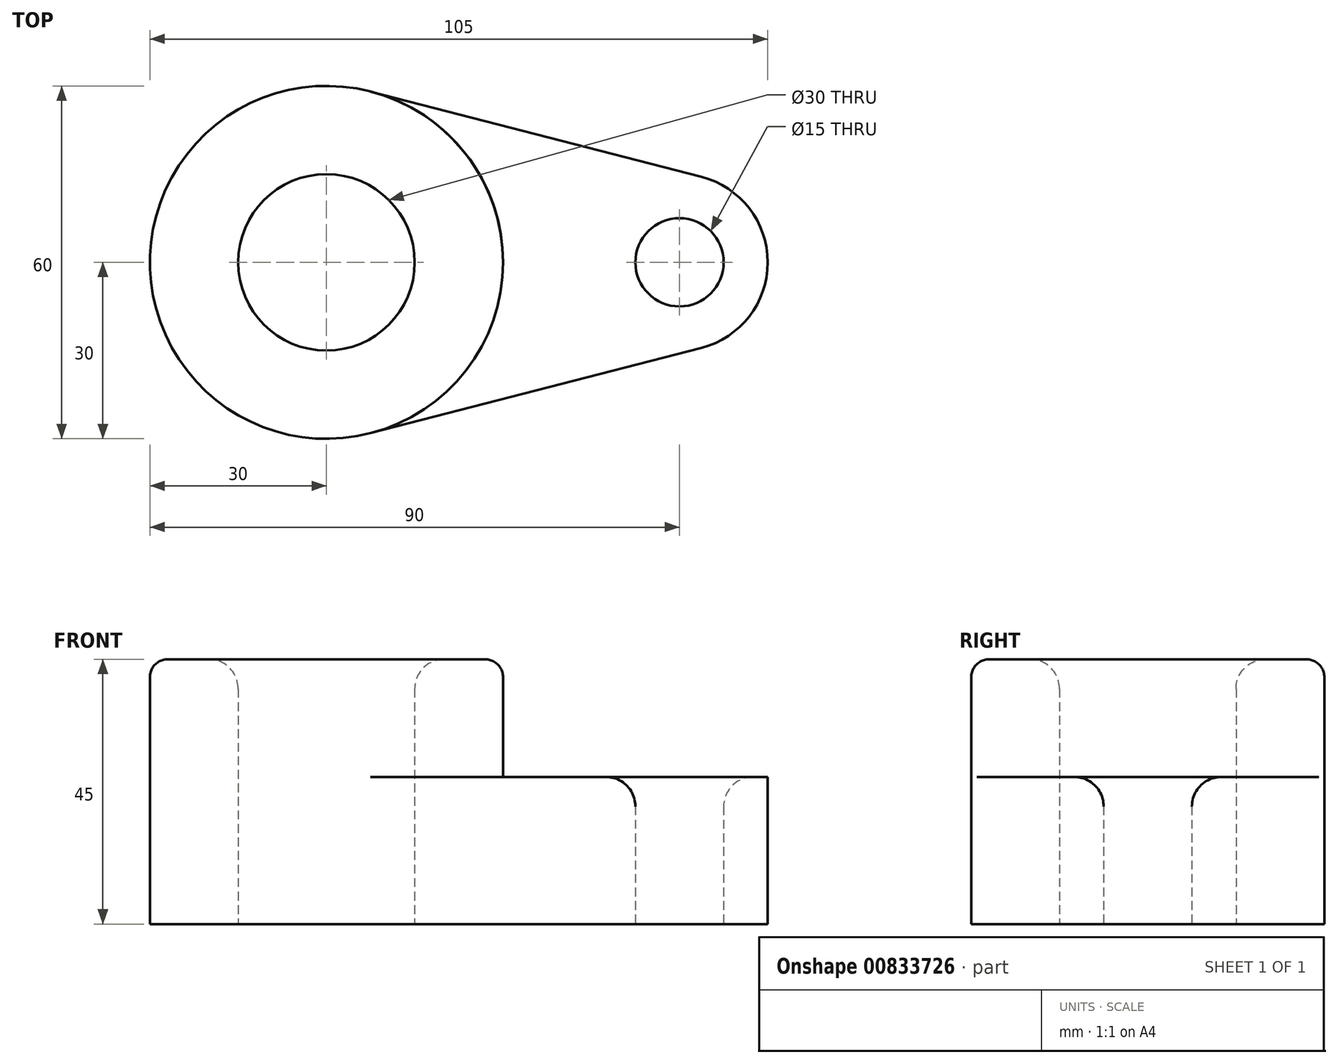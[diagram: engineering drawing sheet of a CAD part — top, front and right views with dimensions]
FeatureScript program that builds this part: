
annotation { "Feature Type Name" : "Feature", "Feature Type Description" : "" }
export const myFeature = defineFeature(function(context is Context, id is Id, definition is map)
    precondition{}
    {
        {
            var Q0;
            Q0=qCreatedBy(makeId("Top.planeOp"),FACE);
            var sketch = newSketch(context, id + "F0", { "sketchPlane" : qUnion([Q0])});
            skCircle(sketch, "E0", {"center": v(0, 0) * mm, "radius": 30 * mm});
            skCircle(sketch, "E1", {"center": v(60, 0) * mm, "radius": 15 * mm});
            skLineSegment(sketch, "E2", {"start": v(7.5, 29.05) * mm, "end": v(63.75, 14.52) * mm});
            skLineSegment(sketch, "E3", {"start": v(7.5, -29.05) * mm, "end": v(63.75, -14.52) * mm});
            skCircle(sketch, "E4", {"center": v(0, 0) * mm, "radius": 15 * mm});
            skCircle(sketch, "E5", {"center": v(60, 0) * mm, "radius": 7.5 * mm});
            skSolve(sketch);
        }
        {
            var Q0;
            Q0=makeQuery(id+"F0.imprint","IMPRINT",FACE,{"disambiguationData":[TD([[makeQuery(id+"F0.imprint","IMPRINT",EDGE,{"derivedFrom":sQuery(id+"F0.wireOp",EDGE,"E4")}),-1.0]])]});
            var Q1;
            {var subQ0=sQuery(id+"F0.wireOp",EDGE,"E2");Q1=makeQuery(id+"F0.imprint","IMPRINT",FACE,{"disambiguationData":[TD([[makeQuery(id+"F0.imprint","IMPRINT",EDGE,{"derivedFrom":subQ0}),-1.0]])]});}
            var Q2;
            Q2=makeQuery(id+"F0.imprint","IMPRINT",FACE,{"disambiguationData":[TD([[makeQuery(id+"F0.imprint","IMPRINT",EDGE,{"derivedFrom":sQuery(id+"F0.wireOp",EDGE,"E5")}),-1.0]])]});
            extrude(context, id + "F1", {"entities" : qUnion([Q0, Q1, Q2]), "depth" : 25 * mm, "offsetDistance" : 25 * mm});
        }
        {
            var Q0;
            Q0=makeQuery(id+"F0.imprint","IMPRINT",FACE,{"disambiguationData":[TD([[makeQuery(id+"F0.imprint","IMPRINT",EDGE,{"derivedFrom":sQuery(id+"F0.wireOp",EDGE,"E4")}),-1.0]])]});
            extrude(context, id + "F2", {"entities" : qUnion([Q0]), "operationType" : NewBodyOperationType.ADD, "depth" : 45 * mm, "offsetDistance" : 25 * mm});
        }
        {
            var Q0;
            Q0=makeQuery(id+"F2.opExtrude","CAP_EDGE",EDGE,{"disambiguationData":[OSD([sQuery(id+"F0.wireOp",EDGE,"E0")])],"isStart":false});
            fillet(context, id + "F3", {"entities" : qUnion([Q0]), "radius" : 3 * mm, "tangentPropagation" : true, "allowEdgeOverflow" : false});
        }
        {
            var Q0;
            Q0=makeQuery(id+"F2.opExtrude","CAP_EDGE",EDGE,{"disambiguationData":[OSD([sQuery(id+"F0.wireOp",EDGE,"E4")])],"isStart":false});
            var Q1;
            Q1=makeQuery(id+"F1.opExtrude","CAP_EDGE",EDGE,{"disambiguationData":[OSD([sQuery(id+"F0.wireOp",EDGE,"E5")])],"isStart":false});
            fillet(context, id + "F4", {"entities" : qUnion([Q0, Q1]), "radius" : 5 * mm, "tangentPropagation" : true, "allowEdgeOverflow" : false});
        }
    });
